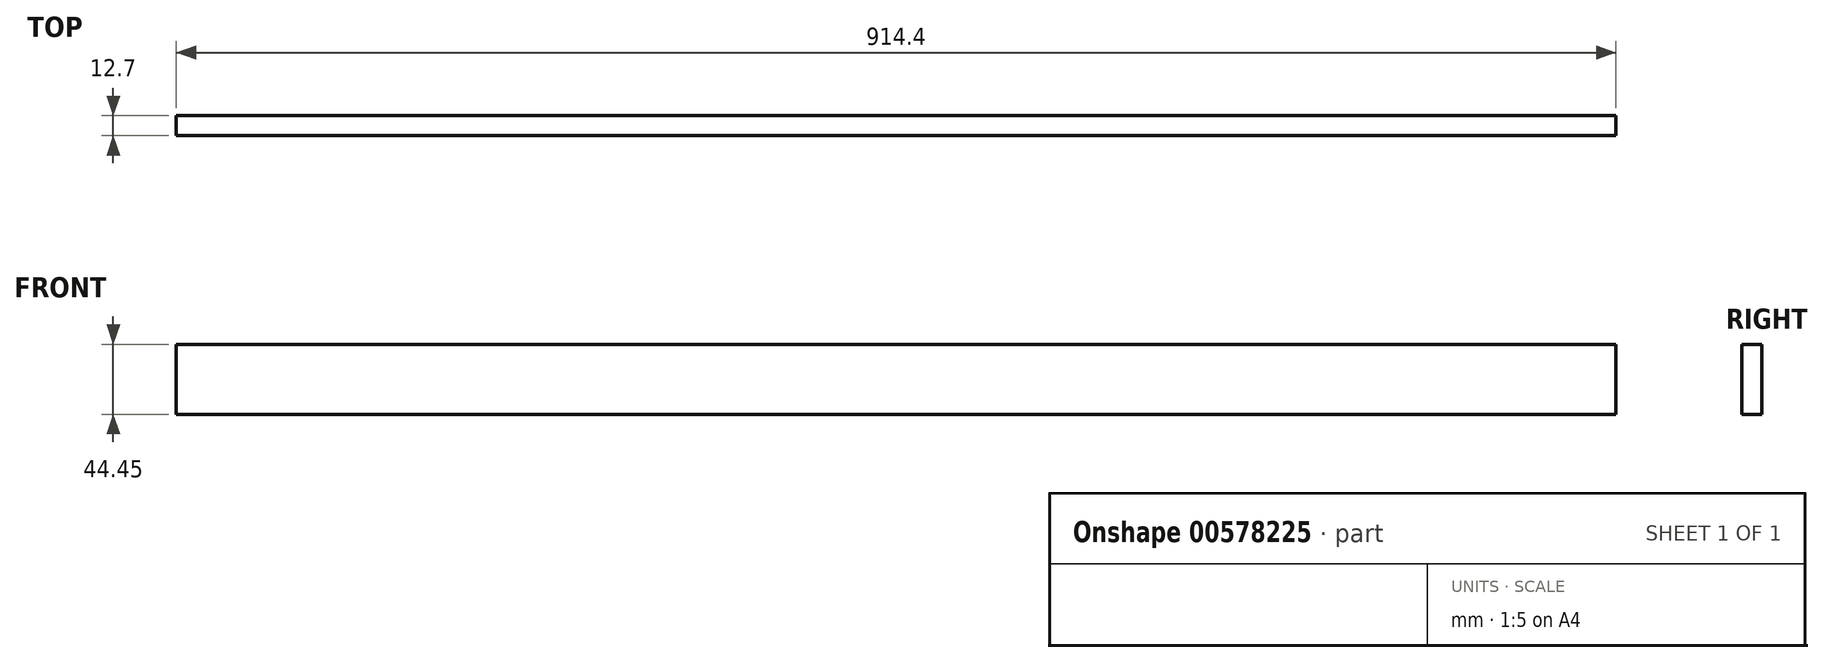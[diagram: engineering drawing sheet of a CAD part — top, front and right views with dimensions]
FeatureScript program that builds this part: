
annotation { "Feature Type Name" : "Feature", "Feature Type Description" : "" }
export const myFeature = defineFeature(function(context is Context, id is Id, definition is map)
    precondition{}
    {
        {
            var Q0;
            Q0=qCreatedBy(makeId("Front.planeOp"),FACE);
            var sketch = newSketch(context, id + "F0", { "sketchPlane" : qUnion([Q0])});
            skLineSegment(sketch, "E0.bottom", {"start": v(-440.01, -90.79) * mm, "end": v(474.39, -90.79) * mm});
            skLineSegment(sketch, "E0.top", {"start": v(-440.01, -135.24) * mm, "end": v(474.39, -135.24) * mm});
            skLineSegment(sketch, "E0.left", {"start": v(-440.01, -90.79) * mm, "end": v(-440.01, -135.24) * mm});
            skLineSegment(sketch, "E0.right", {"start": v(474.39, -90.79) * mm, "end": v(474.39, -135.24) * mm});
            skSolve(sketch);
        }
        {
            var Q0;
            Q0 = qSketchRegion(id + "F0", true);
            extrude(context, id + "F1", {"entities" : qUnion([Q0]), "depth" : 12.7 * mm, "offsetDistance" : 25.4 * mm});
        }
    });
